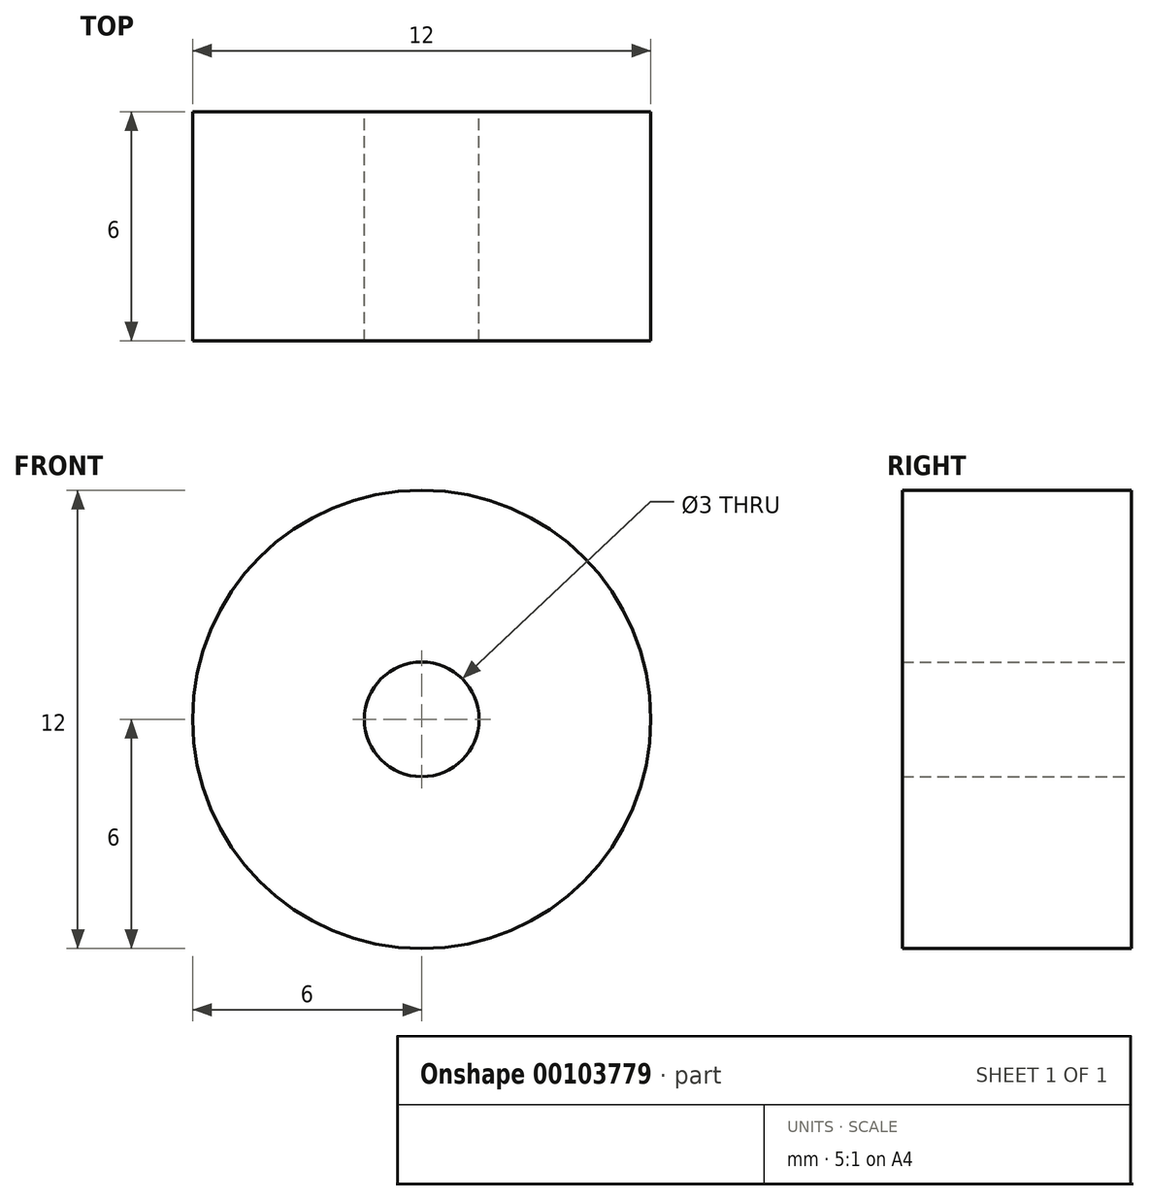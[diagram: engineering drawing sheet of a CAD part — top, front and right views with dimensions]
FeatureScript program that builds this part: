
annotation { "Feature Type Name" : "Feature", "Feature Type Description" : "" }
export const myFeature = defineFeature(function(context is Context, id is Id, definition is map)
    precondition{}
    {
        {
            var Q0;
            Q0=qCreatedBy(makeId("Front.planeOp"),FACE);
            var sketch = newSketch(context, id + "F0", { "sketchPlane" : qUnion([Q0])});
            skCircle(sketch, "E0", {"center": v(0, 0) * mm, "radius": 6 * mm});
            skCircle(sketch, "E1", {"center": v(0, 0) * mm, "radius": 1.5 * mm});
            skSolve(sketch);
        }
        {
            var Q0;
            Q0=makeQuery(id+"F0.imprint","IMPRINT",FACE,{"disambiguationData":[TD([[makeQuery(id+"F0.imprint","IMPRINT",EDGE,{"derivedFrom":sQuery(id+"F0.wireOp",EDGE,"E0")}),1.0]])]});
            extrude(context, id + "F1", {"entities" : qUnion([Q0]), "depth" : 6 * mm, "symmetric" : true});
        }
    });
